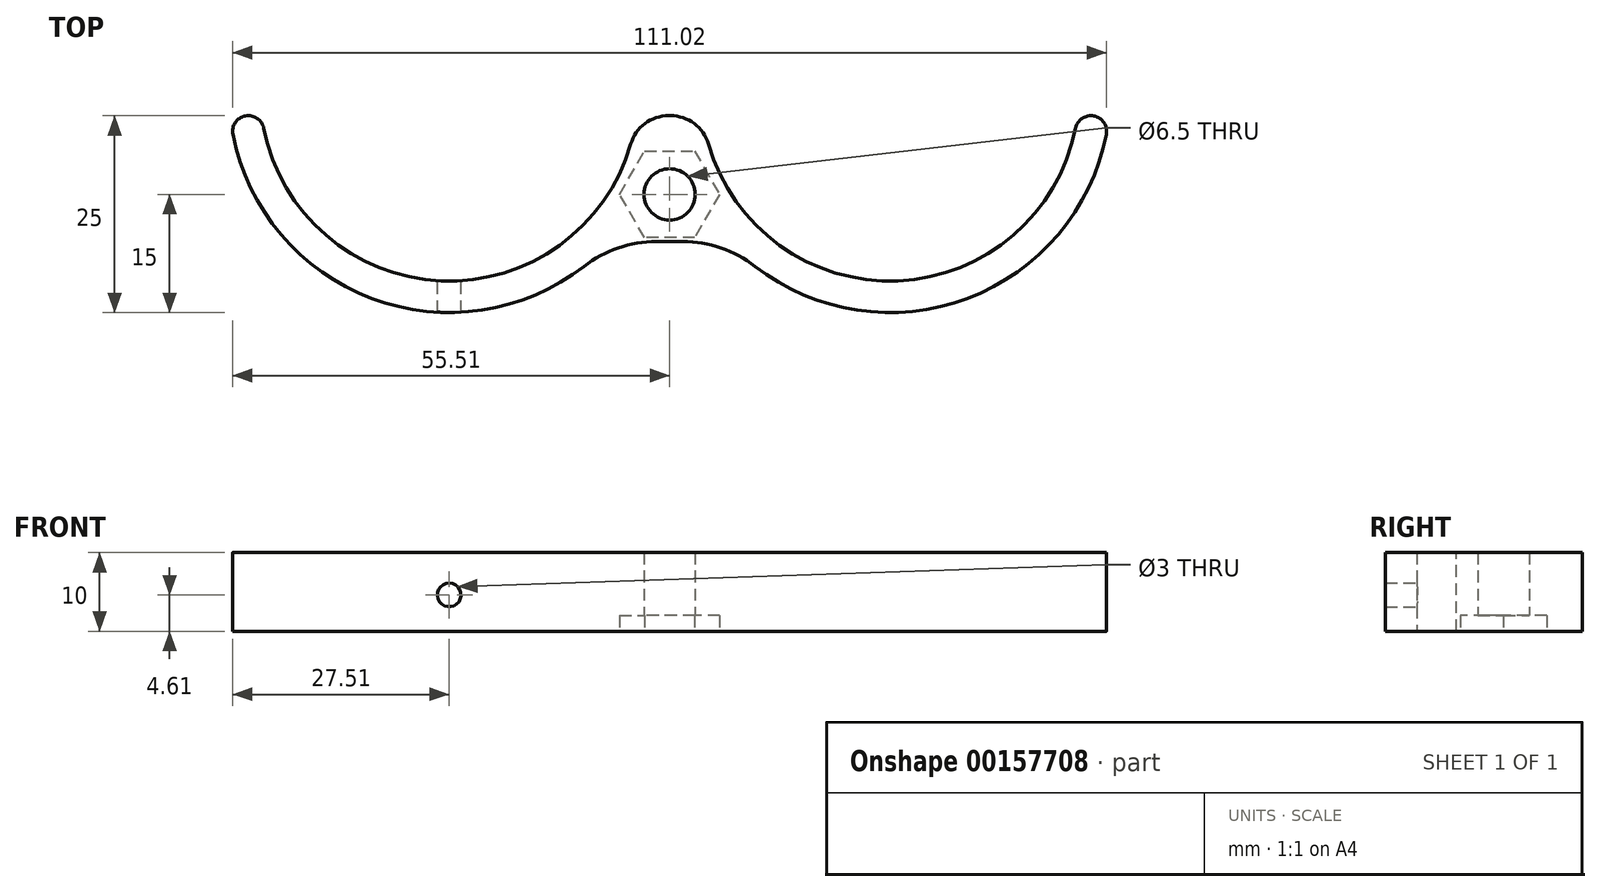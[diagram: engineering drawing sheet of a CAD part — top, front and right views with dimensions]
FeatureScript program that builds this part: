
annotation { "Feature Type Name" : "Feature", "Feature Type Description" : "" }
export const myFeature = defineFeature(function(context is Context, id is Id, definition is map)
    precondition{}
    {
        {
            var Q0;
            Q0=qCreatedBy(makeId("Top.planeOp"),FACE);
            var sketch = newSketch(context, id + "F0", { "sketchPlane" : qUnion([Q0])});
            skLineSegment(sketch, "E0", {"start": v(0, 0) * mm, "end": v(0, 10) * mm});
            skLineSegment(sketch, "E1", {"start": v(0, 10) * mm, "end": v(-8, 10) * mm});
            skLineSegment(sketch, "E2", {"start": v(-8, 10) * mm, "end": v(-8, 0) * mm});
            skLineSegment(sketch, "E3.MirrorCS", {"start": v(4, 10) * mm, "end": v(8, 10) * mm});
            skLineSegment(sketch, "E4.MirrorCS", {"start": v(8, 10) * mm, "end": v(8, 0) * mm});
            skLineSegment(sketch, "E5", {"start": v(4, 10) * mm, "end": v(4, 0) * mm});
            skLineSegment(sketch, "E6", {"start": v(0, 0) * mm, "end": v(0, 0) * mm});
            skPoint(sketch, "E7", {"position": v(4, 10) * mm});
            skPoint(sketch, "E8.orphan", {"position": v(0, 10) * mm});
            skLineSegment(sketch, "E9.bottom", {"start": v(-8, 10) * mm, "end": v(0, 10) * mm});
            skLineSegment(sketch, "E9.top", {"start": v(-8, 12) * mm, "end": v(0, 12) * mm});
            skLineSegment(sketch, "E9.left", {"start": v(-8, 10) * mm, "end": v(-8, 12) * mm});
            skLineSegment(sketch, "E9.right", {"start": v(0, 10) * mm, "end": v(0, 12) * mm});
            skLineSegment(sketch, "E10.bottom", {"start": v(-8, 12) * mm, "end": v(8, 12) * mm});
            skLineSegment(sketch, "E10.top", {"start": v(-8, 60) * mm, "end": v(8, 60) * mm});
            skLineSegment(sketch, "E10.left", {"start": v(-8, 12) * mm, "end": v(-8, 60) * mm});
            skLineSegment(sketch, "E10.right", {"start": v(8, 12) * mm, "end": v(8, 60) * mm});
            skLineSegment(sketch, "E11", {"start": v(-8, 17) * mm, "end": v(8, 17) * mm});
            skLineSegment(sketch, "E12", {"start": v(-8, 36) * mm, "end": v(8, 36) * mm, "construction": true});
            skLineSegment(sketch, "E13.MirrorCS", {"start": v(-8, 55) * mm, "end": v(8, 55) * mm});
            skCircle(sketch, "E14", {"center": v(0, 55) * mm, "radius": 1.5 * mm});
            skCircle(sketch, "E15.MirrorC", {"center": v(0, 17) * mm, "radius": 1.5 * mm});
            skCircle(sketch, "E16", {"center": v(0, 55) * mm, "radius": 2.25 * mm});
            skCircle(sketch, "E17.MirrorC", {"center": v(0, 17) * mm, "radius": 2.25 * mm});
            skLineSegment(sketch, "E18", {"start": v(8, 10) * mm, "end": v(8, 12) * mm});
            skCircle(sketch, "E19", {"center": v(-28, -27) * mm, "radius": 24 * mm});
            skLineSegment(sketch, "E20.bottom", {"start": v(8, 0) * mm, "end": v(-8, 0) * mm});
            skLineSegment(sketch, "E20.top", {"start": v(8, 0) * mm, "end": v(-8, 0) * mm});
            skLineSegment(sketch, "E20.left", {"start": v(8, 0) * mm, "end": v(8, 0) * mm});
            skLineSegment(sketch, "E20.right", {"start": v(-8, 0) * mm, "end": v(-8, 0) * mm});
            skLineSegment(sketch, "E21.bottom", {"start": v(-8, -46) * mm, "end": v(8, -46) * mm});
            skLineSegment(sketch, "E21.top", {"start": v(-8, 0) * mm, "end": v(8, 0) * mm});
            skLineSegment(sketch, "E21.left", {"start": v(-8, -46) * mm, "end": v(-8, 0) * mm});
            skLineSegment(sketch, "E21.right", {"start": v(8, -46) * mm, "end": v(8, 0) * mm});
            skCircle(sketch, "E22.0", {"center": v(-28, -27) * mm, "radius": 28 * mm});
            skLineSegment(sketch, "E23", {"start": v(-72.4, -30) * mm, "end": v(72.93, -30) * mm, "construction": true});
            skCircle(sketch, "E24.MirrorC", {"center": v(28, -27) * mm, "radius": 28 * mm});
            skCircle(sketch, "E25.MirrorC", {"center": v(28, -27) * mm, "radius": 24 * mm});
            skLineSegment(sketch, "E26", {"start": v(-55.84, -30) * mm, "end": v(-51.81, -30) * mm});
            skLineSegment(sketch, "E27", {"start": v(51.81, -30) * mm, "end": v(55.84, -30) * mm});
            skCircle(sketch, "E28", {"center": v(0, -40) * mm, "radius": 3.25 * mm});
            skLineSegment(sketch, "E29", {"start": v(-4.19, -30) * mm, "end": v(4.19, -30) * mm});
            skCircle(sketch, "E30.cCircle", {"center": v(0, -40) * mm, "radius": 5.5 * mm, "construction": true});
            skLineSegment(sketch, "E30.0", {"start": v(3.18, -45.5) * mm, "end": v(-3.18, -45.5) * mm});
            skLineSegment(sketch, "E30.1", {"start": v(-3.18, -45.5) * mm, "end": v(-6.35, -40) * mm});
            skLineSegment(sketch, "E30.2", {"start": v(-6.35, -40) * mm, "end": v(-3.18, -34.5) * mm});
            skLineSegment(sketch, "E30.3", {"start": v(-3.18, -34.5) * mm, "end": v(3.18, -34.5) * mm});
            skLineSegment(sketch, "E30.4", {"start": v(3.18, -34.5) * mm, "end": v(6.35, -40) * mm});
            skLineSegment(sketch, "E30.5", {"start": v(6.35, -40) * mm, "end": v(3.18, -45.5) * mm});
            skPoint(sketch, "E30.0.midPoint", {"position": v(0, -45.5) * mm});
            skLineSegment(sketch, "E31", {"start": v(-3.8, -44.43) * mm, "end": v(-2.89, -46) * mm});
            skLineSegment(sketch, "E32", {"start": v(3.92, -44.21) * mm, "end": v(2.89, -46) * mm});
            skSolve(sketch);
        }
        {
            var Q0;
            {var subQ3=sQuery(id+"F0.wireOp",EDGE,"E6");Q0=makeQuery(id+"F0.imprint","IMPRINT",FACE,{"disambiguationData":[TD([[makeQuery(id+"F0.imprint","IMPRINT",EDGE,{"derivedFrom":subQ3}),1.0]])]});}
            var Q1;
            {var subQ0=sQuery(id+"F0.wireOp",EDGE,"E6");Q1=makeQuery(id+"F0.imprint","IMPRINT",FACE,{"disambiguationData":[TD([[makeQuery(id+"F0.imprint","IMPRINT",EDGE,{"derivedFrom":subQ0}),-1.0]])]});}
            var Q2;
            {var subQ0=sQuery(id+"F0.wireOp",EDGE,"E22.0");var subQ1=sQuery(id+"F0.wireOp",EDGE,"E21.bottom");var subQ2=makeQuery(id+"F0.imprint","INTERSECT",VERTEX,{"derivedFrom":[subQ1,subQ0]});Q2=makeQuery(id+"F0.imprint","IMPRINT",FACE,{"disambiguationData":[TD([[makeQuery(id+"F0.imprint","IMPRINT",EDGE,{"disambiguationData":[TD([[subQ2,-1.0]])],"derivedFrom":subQ1}),1.0]])]});}
            var Q3;
            {var subQ0=sQuery(id+"F0.wireOp",EDGE,"E21.right");var subQ1=sQuery(id+"F0.wireOp",EDGE,"E21.bottom");var subQ2=makeQuery(id+"F0.imprint","INTERSECT",VERTEX,{"derivedFrom":[subQ1,subQ0]});Q3=makeQuery(id+"F0.imprint","IMPRINT",FACE,{"disambiguationData":[TD([[makeQuery(id+"F0.imprint","IMPRINT",EDGE,{"disambiguationData":[TD([[subQ2,1.0]])],"derivedFrom":subQ1}),1.0]])]});}
            var Q4;
            {var subQ0=sQuery(id+"F0.wireOp",EDGE,"E26");Q4=makeQuery(id+"F0.imprint","IMPRINT",FACE,{"disambiguationData":[TD([[makeQuery(id+"F0.imprint","IMPRINT",EDGE,{"derivedFrom":subQ0}),-1.0]])]});}
            var Q5;
            {var subQ0=sQuery(id+"F0.wireOp",EDGE,"E27");Q5=makeQuery(id+"F0.imprint","IMPRINT",FACE,{"disambiguationData":[TD([[makeQuery(id+"F0.imprint","IMPRINT",EDGE,{"derivedFrom":subQ0}),-1.0]])]});}
            var Q6;
            {var subQ7=sQuery(id+"F0.wireOp",EDGE,"E19");var subQ9=sQuery(id+"F0.wireOp",EDGE,"E29");var subQ10=makeQuery(id+"F0.imprint","INTERSECT",VERTEX,{"derivedFrom":[subQ7,subQ9]});Q6=makeQuery(id+"F0.imprint","IMPRINT",FACE,{"disambiguationData":[TD([[makeQuery(id+"F0.imprint","IMPRINT",EDGE,{"disambiguationData":[TD([[subQ10,1.0]])],"derivedFrom":subQ7}),-1.0]])]});}
            var Q7;
            {var subQ0=sQuery(id+"F0.wireOp",EDGE,"E28");var subQ1=sQuery(id+"F0.wireOp",EDGE,"E22.0");var subQ2=makeQuery(id+"F0.imprint","INTERSECT",VERTEX,{"disambiguationData":[OD(1.0)],"derivedFrom":[subQ1,subQ0]});Q7=makeQuery(id+"F0.imprint","IMPRINT",FACE,{"disambiguationData":[TD([[makeQuery(id+"F0.imprint","IMPRINT",EDGE,{"disambiguationData":[TD([[subQ2,-1.0]])],"derivedFrom":subQ1}),-1.0]])]});}
            var Q8;
            {var subQ0=sQuery(id+"F0.wireOp",EDGE,"E32");var subQ6=sQuery(id+"F0.wireOp",EDGE,"E21.bottom");var subQ8=makeQuery(id+"F0.imprint","INTERSECT",VERTEX,{"derivedFrom":[subQ6,subQ0]});Q8=makeQuery(id+"F0.imprint","IMPRINT",FACE,{"disambiguationData":[TD([[makeQuery(id+"F0.imprint","IMPRINT",EDGE,{"disambiguationData":[TD([[subQ8,-1.0]])],"derivedFrom":subQ6}),1.0]])]});}
            var Q9;
            {var subQ0=sQuery(id+"F0.wireOp",EDGE,"E30.2");Q9=makeQuery(id+"F0.imprint","IMPRINT",FACE,{"disambiguationData":[TD([[makeQuery(id+"F0.imprint","IMPRINT",EDGE,{"derivedFrom":subQ0}),-1.0]])]});}
            var Q10;
            {var subQ0=sQuery(id+"F0.wireOp",EDGE,"E30.3");var subQ1=sQuery(id+"F0.wireOp",EDGE,"E22.0");var subQ2=makeQuery(id+"F0.imprint","INTERSECT",VERTEX,{"derivedFrom":[subQ1,subQ0]});Q10=makeQuery(id+"F0.imprint","IMPRINT",FACE,{"disambiguationData":[TD([[makeQuery(id+"F0.imprint","IMPRINT",EDGE,{"disambiguationData":[TD([[subQ2,-1.0]])],"derivedFrom":subQ1}),-1.0]])]});}
            var Q11;
            {var subQ0=sQuery(id+"F0.wireOp",EDGE,"E30.4");Q11=makeQuery(id+"F0.imprint","IMPRINT",FACE,{"disambiguationData":[TD([[makeQuery(id+"F0.imprint","IMPRINT",EDGE,{"derivedFrom":subQ0}),-1.0]])]});}
            var Q12;
            {var subQ0=sQuery(id+"F0.wireOp",EDGE,"E30.0");Q12=makeQuery(id+"F0.imprint","IMPRINT",FACE,{"disambiguationData":[TD([[makeQuery(id+"F0.imprint","IMPRINT",EDGE,{"derivedFrom":subQ0}),-1.0]])]});}
            var Q13;
            {var subQ5=sQuery(id+"F0.wireOp",EDGE,"E30.0");Q13=makeQuery(id+"F0.imprint","IMPRINT",FACE,{"disambiguationData":[TD([[makeQuery(id+"F0.imprint","IMPRINT",EDGE,{"derivedFrom":subQ5}),1.0]])]});}
            extrude(context, id + "F1", {"entities" : qUnion([Q0, Q1, Q2, Q3, Q4, Q5, Q6, Q7, Q8, Q9, Q10, Q11, Q12, Q13]), "depth" : 10 * mm, "offsetDistance" : 25 * mm});
        }
        {
            var Q0;
            Q0=makeQuery(id+"F1.opExtrude","SWEPT_EDGE",EDGE,{"disambiguationData":[OSD([sQuery(id+"F0.wireOp",EDGE,"E19"),sQuery(id+"F0.wireOp",EDGE,"E29")])]});
            var Q1;
            Q1=makeQuery(id+"F1.opExtrude","SWEPT_EDGE",EDGE,{"disambiguationData":[OSD([sQuery(id+"F0.wireOp",EDGE,"E25.MirrorC"),sQuery(id+"F0.wireOp",EDGE,"E29")])]});
            fillet(context, id + "F2", {"entities" : qUnion([Q0, Q1]), "radius" : 5 * mm, "tangentPropagation" : true, "allowEdgeOverflow" : false});
        }
        {
            var Q0;
            Q0=makeQuery(id+"F1.opExtrude","SWEPT_EDGE",EDGE,{"disambiguationData":[OSD([sQuery(id+"F0.wireOp",EDGE,"E21.bottom"),sQuery(id+"F0.wireOp",EDGE,"E22.0")])]});
            var Q1;
            Q1=makeQuery(id+"F1.opExtrude","SWEPT_EDGE",EDGE,{"disambiguationData":[OSD([sQuery(id+"F0.wireOp",EDGE,"E21.bottom"),sQuery(id+"F0.wireOp",EDGE,"E24.MirrorC")])]});
            fillet(context, id + "F3", {"entities" : qUnion([Q0, Q1]), "radius" : 15 * mm, "tangentPropagation" : true, "allowEdgeOverflow" : false});
        }
        {
            var Q0;
            Q0=makeQuery(id+"F1.opExtrude","SWEPT_EDGE",EDGE,{"disambiguationData":[OSD([sQuery(id+"F0.wireOp",EDGE,"E22.0"),sQuery(id+"F0.wireOp",EDGE,"E26")])]});
            var Q1;
            Q1=makeQuery(id+"F1.opExtrude","SWEPT_EDGE",EDGE,{"disambiguationData":[OSD([sQuery(id+"F0.wireOp",EDGE,"E19"),sQuery(id+"F0.wireOp",EDGE,"E26")])]});
            var Q2;
            Q2=makeQuery(id+"F1.opExtrude","SWEPT_EDGE",EDGE,{"disambiguationData":[OSD([sQuery(id+"F0.wireOp",EDGE,"E25.MirrorC"),sQuery(id+"F0.wireOp",EDGE,"E27")])]});
            var Q3;
            Q3=makeQuery(id+"F1.opExtrude","SWEPT_EDGE",EDGE,{"disambiguationData":[OSD([sQuery(id+"F0.wireOp",EDGE,"E24.MirrorC"),sQuery(id+"F0.wireOp",EDGE,"E27")])]});
            fillet(context, id + "F4", {"entities" : qUnion([Q0, Q1, Q2, Q3]), "radius" : 2 * mm, "tangentPropagation" : true, "allowEdgeOverflow" : false});
        }
        {
            var Q0;
            Q0=qCreatedBy(makeId("Front.planeOp"),FACE);
            var sketch = newSketch(context, id + "F5", { "sketchPlane" : qUnion([Q0])});
            skCircle(sketch, "E33", {"center": v(-28, 4.61) * mm, "radius": 1.5 * mm});
            skCircle(sketch, "E34.MirrorC", {"center": v(28, 4.61) * mm, "radius": 1.5 * mm});
            skSolve(sketch);
        }
        {
            var Q0;
            Q0=makeQuery(id+"F5.imprint","IMPRINT",FACE,{"disambiguationData":[TD([[makeQuery(id+"F5.imprint","IMPRINT",EDGE,{"derivedFrom":sQuery(id+"F5.wireOp",EDGE,"E33")}),1.0]])]});
            var Q1;
            Q1=makeQuery(id+"F5.imprint","IMPRINT",FACE,{"disambiguationData":[TD([[makeQuery(id+"F5.imprint","IMPRINT",EDGE,{"derivedFrom":sQuery(id+"F5.wireOp",EDGE,"E34.MirrorC")}),-1.0]])]});
            extrude(context, id + "F6", {"entities" : qUnion([Q0, Q1]), "operationType" : NewBodyOperationType.REMOVE, "depth" : 70 * mm, "offsetDistance" : 25 * mm});
        }
        {
            var Q0;
            {var subQ0=sQuery(id+"F0.wireOp",EDGE,"E30.4");Q0=makeQuery(id+"F0.imprint","IMPRINT",FACE,{"disambiguationData":[TD([[makeQuery(id+"F0.imprint","IMPRINT",EDGE,{"derivedFrom":subQ0}),-1.0]])]});}
            var Q1;
            {var subQ0=sQuery(id+"F0.wireOp",EDGE,"E28");var subQ1=sQuery(id+"F0.wireOp",EDGE,"E22.0");var subQ2=makeQuery(id+"F0.imprint","INTERSECT",VERTEX,{"disambiguationData":[OD(1.0)],"derivedFrom":[subQ1,subQ0]});Q1=makeQuery(id+"F0.imprint","IMPRINT",FACE,{"disambiguationData":[TD([[makeQuery(id+"F0.imprint","IMPRINT",EDGE,{"disambiguationData":[TD([[subQ2,-1.0]])],"derivedFrom":subQ1}),-1.0]])]});}
            var Q2;
            {var subQ0=sQuery(id+"F0.wireOp",EDGE,"E30.2");Q2=makeQuery(id+"F0.imprint","IMPRINT",FACE,{"disambiguationData":[TD([[makeQuery(id+"F0.imprint","IMPRINT",EDGE,{"derivedFrom":subQ0}),-1.0]])]});}
            var Q3;
            {var subQ0=sQuery(id+"F0.wireOp",EDGE,"E30.0");Q3=makeQuery(id+"F0.imprint","IMPRINT",FACE,{"disambiguationData":[TD([[makeQuery(id+"F0.imprint","IMPRINT",EDGE,{"derivedFrom":subQ0}),-1.0]])]});}
            extrude(context, id + "F7", {"entities" : qUnion([Q0, Q1, Q2, Q3]), "operationType" : NewBodyOperationType.REMOVE, "depth" : 2 * mm, "offsetDistance" : 25 * mm});
        }
    });
